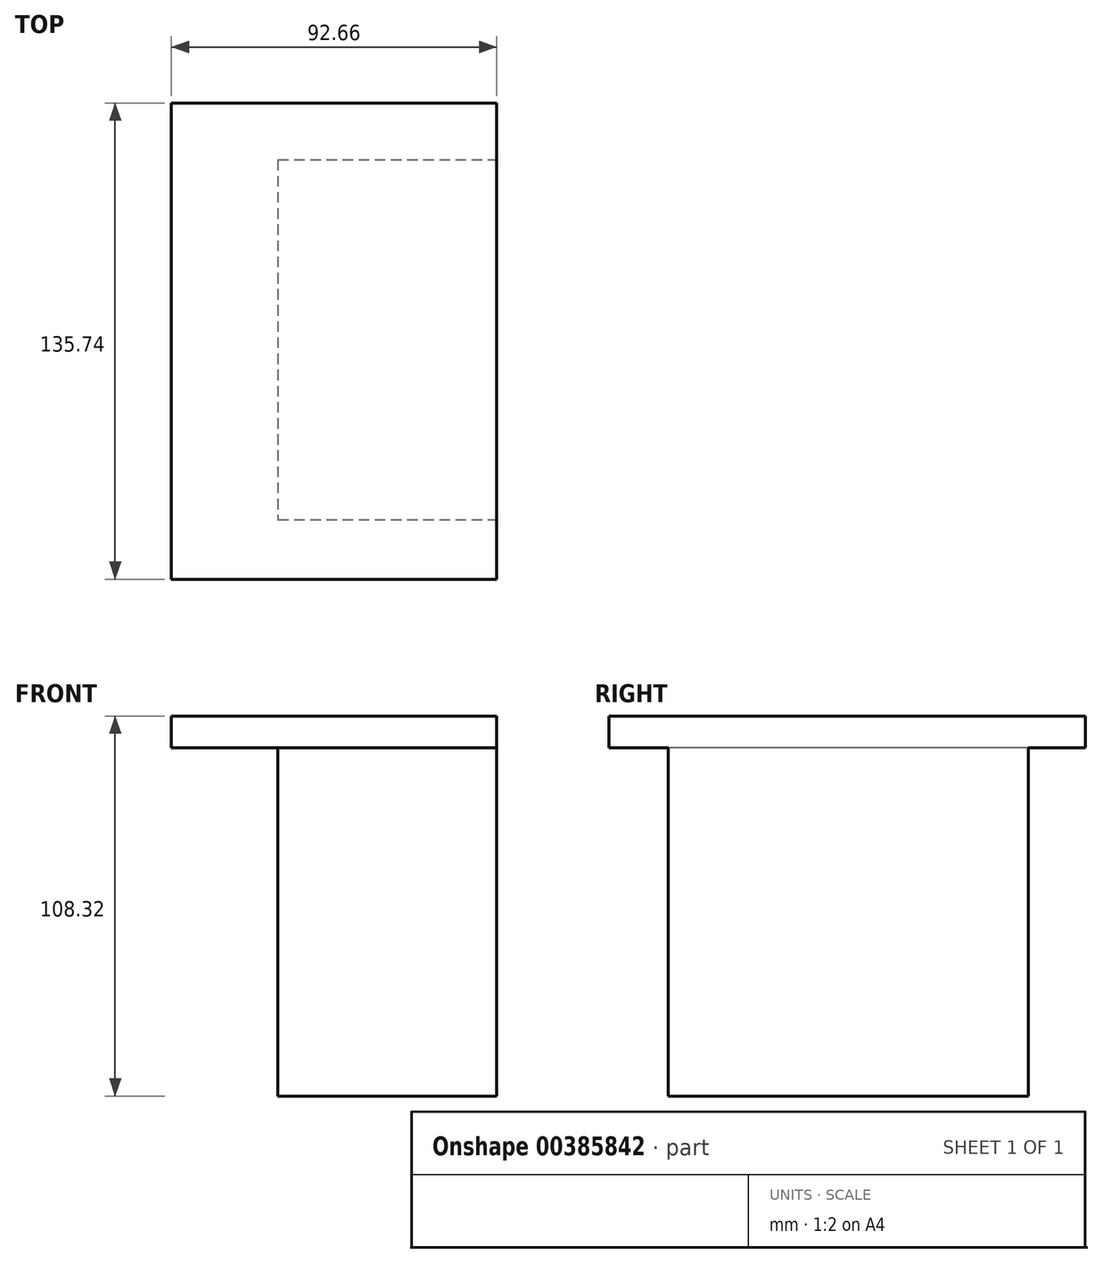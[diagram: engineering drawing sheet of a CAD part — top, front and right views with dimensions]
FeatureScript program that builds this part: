
annotation { "Feature Type Name" : "Feature", "Feature Type Description" : "" }
export const myFeature = defineFeature(function(context is Context, id is Id, definition is map)
    precondition{}
    {
        {
            var Q0;
            Q0=qCreatedBy(makeId("Top.planeOp"),FACE);
            var sketch = newSketch(context, id + "F0", { "sketchPlane" : qUnion([Q0])});
            skLineSegment(sketch, "E0.bottom", {"start": v(-42.85, 69.1) * mm, "end": v(49.81, 69.1) * mm});
            skLineSegment(sketch, "E0.top", {"start": v(-42.85, -66.63) * mm, "end": v(49.81, -66.63) * mm});
            skLineSegment(sketch, "E0.left", {"start": v(-42.85, 69.1) * mm, "end": v(-42.85, -66.63) * mm});
            skLineSegment(sketch, "E0.right", {"start": v(49.81, 69.1) * mm, "end": v(49.81, -66.63) * mm});
            skSolve(sketch);
        }
        {
            var Q0;
            Q0=makeQuery(id+"F0.imprint","IMPRINT",FACE,{"disambiguationData":[TD([[makeQuery(id+"F0.imprint","IMPRINT",EDGE,{"derivedFrom":sQuery(id+"F0.wireOp",EDGE,"E0.bottom")}),-1.0]])]});
            extrude(context, id + "F1", {"entities" : qUnion([Q0]), "depth" : 9 * mm});
        }
        {
            var Q0;
            Q0=makeQuery(id+"F1.opExtrude","CAP_FACE",FACE,{"disambiguationData":[OSD([sQuery(id+"F0.wireOp",EDGE,"E0.bottom"),sQuery(id+"F0.wireOp",EDGE,"E0.top"),sQuery(id+"F0.wireOp",EDGE,"E0.left"),sQuery(id+"F0.wireOp",EDGE,"E0.right")])],"isStart":false});
            var sketch = newSketch(context, id + "F2", { "sketchPlane" : qUnion([Q0])});
            skLineSegment(sketch, "E1.bottom", {"start": v(-12.47, 52.9) * mm, "end": v(49.96, 52.9) * mm});
            skLineSegment(sketch, "E1.top", {"start": v(-12.47, -49.71) * mm, "end": v(49.96, -49.71) * mm});
            skLineSegment(sketch, "E1.left", {"start": v(-12.47, 52.9) * mm, "end": v(-12.47, -49.71) * mm});
            skLineSegment(sketch, "E1.right", {"start": v(49.96, 52.9) * mm, "end": v(49.96, -49.71) * mm});
            skSolve(sketch);
        }
        {
            var Q0;
            {var subQ0=sQuery(id+"F2.wireOp",EDGE,"E1.left");Q0=makeQuery(id+"F2.imprint","IMPRINT",FACE,{"disambiguationData":[TD([[makeQuery(id+"F2.imprint","IMPRINT",EDGE,{"derivedFrom":subQ0}),1.0]])]});}
            extrude(context, id + "F3", {"entities" : qUnion([Q0]), "operationType" : NewBodyOperationType.ADD, "oppositeDirection" : true, "depth" : 108.32 * mm});
        }
    });
